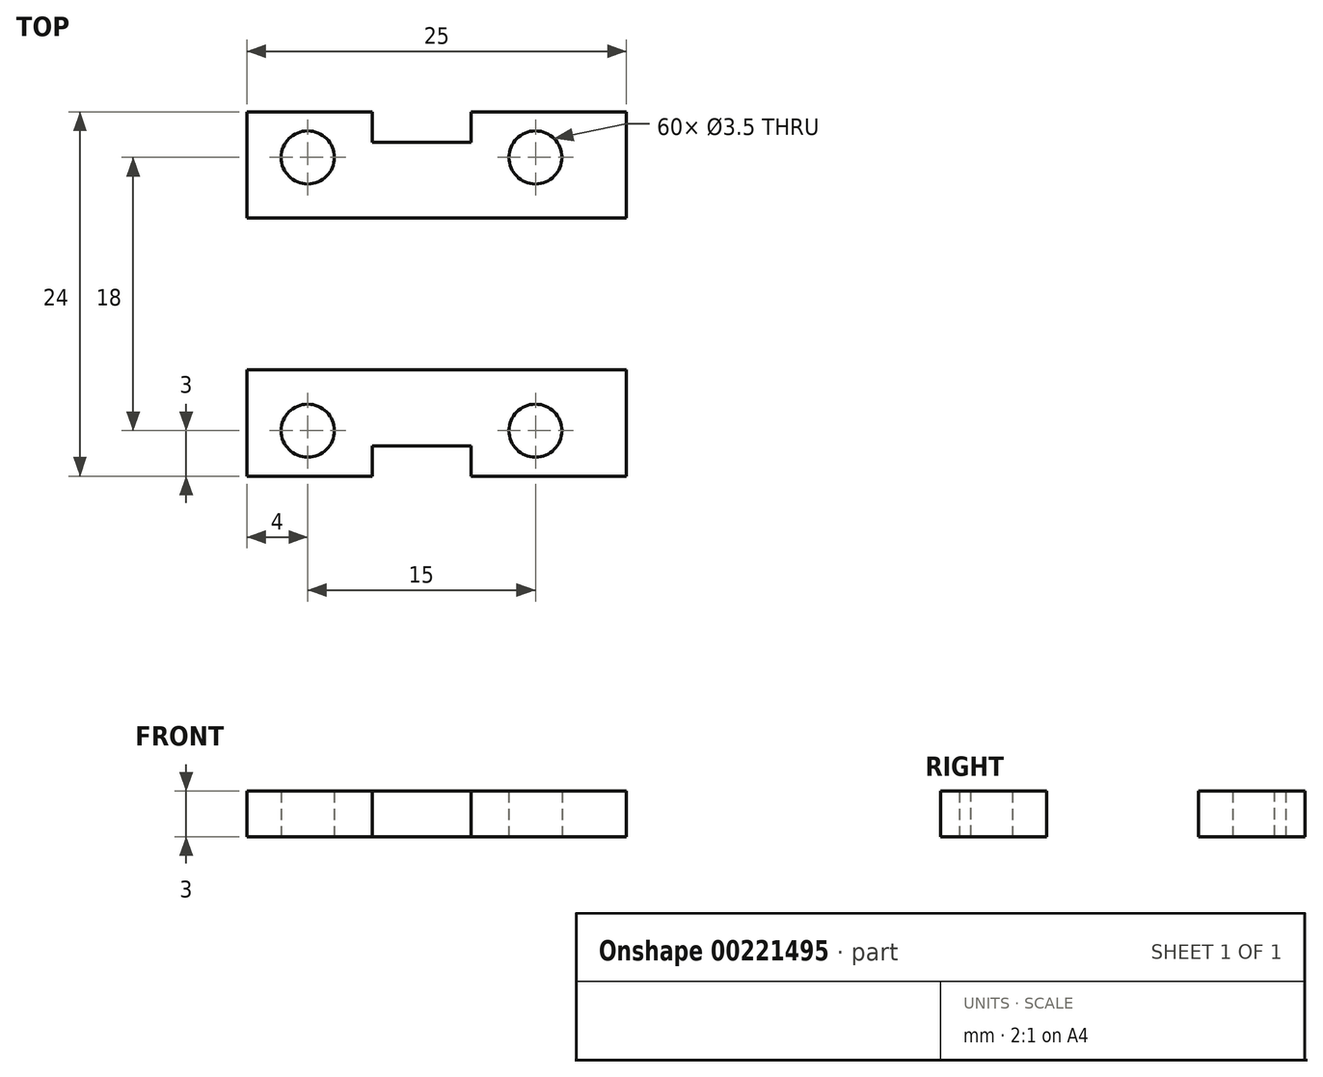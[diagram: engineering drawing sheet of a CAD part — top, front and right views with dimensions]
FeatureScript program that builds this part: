
annotation { "Feature Type Name" : "Feature", "Feature Type Description" : "" }
export const myFeature = defineFeature(function(context is Context, id is Id, definition is map)
    precondition{}
    {
        {
            var Q0;
            Q0=qCreatedBy(makeId("Top.planeOp"),FACE);
            var sketch = newSketch(context, id + "F0", { "sketchPlane" : qUnion([Q0])});
            skLineSegment(sketch, "E0.bottom", {"start": v(0, 0) * mm, "end": v(25, 0) * mm});
            skLineSegment(sketch, "E0.top", {"start": v(0, 7) * mm, "end": v(25, 7) * mm});
            skLineSegment(sketch, "E0.left", {"start": v(0, 0) * mm, "end": v(0, 7) * mm});
            skLineSegment(sketch, "E0.right", {"start": v(25, 0) * mm, "end": v(25, 7) * mm});
            skCircle(sketch, "E1", {"center": v(4, 4) * mm, "radius": 1.75 * mm});
            skCircle(sketch, "E2", {"center": v(19, 4) * mm, "radius": 1.75 * mm});
            skSolve(sketch);
        }
        {
            var Q0;
            Q0 = qSketchRegion(id + "F0", true);
            extrude(context, id + "F1", {"entities" : qUnion([Q0]), "depth" : 3 * mm});
        }
        {
            var Q0;
            Q0=makeQuery(id+"F1.opExtrude","CAP_FACE",FACE,{"disambiguationData":[OSD([sQuery(id+"F0.wireOp",EDGE,"E0.bottom"),sQuery(id+"F0.wireOp",EDGE,"E0.top"),sQuery(id+"F0.wireOp",EDGE,"E0.left"),sQuery(id+"F0.wireOp",EDGE,"E0.right"),sQuery(id+"F0.wireOp",EDGE,"E1"),sQuery(id+"F0.wireOp",EDGE,"E2")])],"isStart":false});
            var sketch = newSketch(context, id + "F2", { "sketchPlane" : qUnion([Q0])});
            skLineSegment(sketch, "E3", {"start": v(4, 4) * mm, "end": v(19, 4) * mm, "construction": true});
            skLineSegment(sketch, "E4.bottom", {"start": v(8.25, 7) * mm, "end": v(14.75, 7) * mm});
            skLineSegment(sketch, "E4.top", {"start": v(8.25, 5) * mm, "end": v(14.75, 5) * mm});
            skLineSegment(sketch, "E4.left", {"start": v(8.25, 7) * mm, "end": v(8.25, 5) * mm});
            skLineSegment(sketch, "E4.right", {"start": v(14.75, 7) * mm, "end": v(14.75, 5) * mm});
            skPoint(sketch, "E5", {"position": v(11.5, 5) * mm});
            skPoint(sketch, "E6", {"position": v(11.5, 4) * mm});
            skSolve(sketch);
        }
        {
            var Q0;
            Q0=makeQuery(id+"F2.imprint","IMPRINT",FACE,{"disambiguationData":[TD([[makeQuery(id+"F2.imprint","IMPRINT",EDGE,{"derivedFrom":sQuery(id+"F2.wireOp",EDGE,"E4.bottom")}),-1.0]])]});
            extrude(context, id + "F3", {"entities" : qUnion([Q0]), "operationType" : NewBodyOperationType.REMOVE, "endBound" : BoundingType.THROUGH_ALL, "oppositeDirection" : true, "depth" : 25 * mm});
        }
        {
            var Q0;
            Q0=makeQuery(id+"F1.opExtrude","SWEPT_FACE",FACE,{"disambiguationData":[OSD([sQuery(id+"F0.wireOp",EDGE,"E0.bottom")])]});
            cPlane(context, id + "F4", {"entities" : qUnion([Q0]), "cplaneType" : CPlaneType.OFFSET, "offset" : 5 * mm, "width" : 150 * mm, "height" : 150 * mm});
        }
        {
            var Q0;
            Q0=makeQuery(id+"F1.opExtrude","SWEPT_BODY",BODY,{"disambiguationData":[OSD([sQuery(id+"F0.wireOp",EDGE,"E0.bottom"),sQuery(id+"F0.wireOp",EDGE,"E0.top"),sQuery(id+"F0.wireOp",EDGE,"E0.left"),sQuery(id+"F0.wireOp",EDGE,"E0.right"),sQuery(id+"F0.wireOp",EDGE,"E1"),sQuery(id+"F0.wireOp",EDGE,"E2")])]});
            var Q1;
            Q1=qCreatedBy(id+"F4.planeOp",FACE);
            mirror(context, id + "F5", {"entities" : qUnion([Q0]), "mirrorPlane" : qUnion([Q1])});
        }
    });
